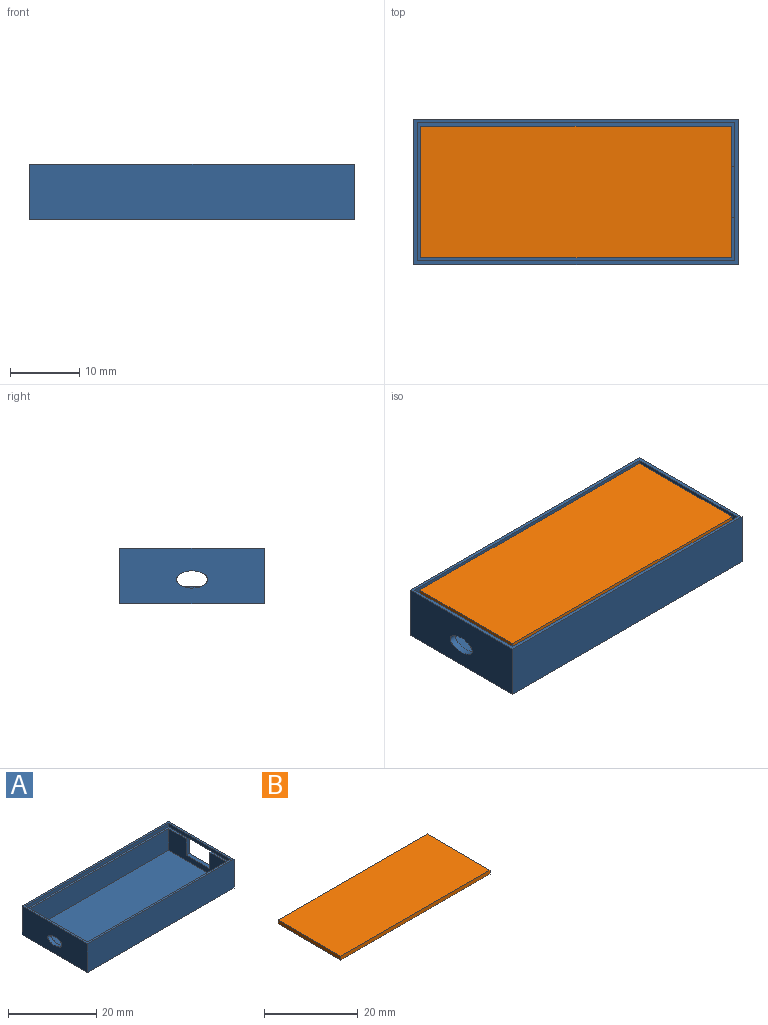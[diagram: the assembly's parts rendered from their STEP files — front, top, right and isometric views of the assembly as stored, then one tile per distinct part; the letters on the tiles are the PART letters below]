
ASSEMBLY  parts=2 mates=1
PART A: 21 faces, bbox 47x21x8 mm
  f0: plane 46x20mm, normal (0,0,1), area 61.3mm2, adj f2,f3,f4,f5,f7,f8,f9,f10
  f1: plane 21x8mm, normal (1,0,0), area 134.2mm2, adj f11,f13,f14,f15,f17,f18,f19,f20
  f2: plane 45x6mm, normal (0,-1,0), area 270mm2, adj f0,f3,f5,f6
  f3: plane 19x6mm, normal (1,0,0), area 105.2mm2, adj f0,f2,f4,f6,f16
  f4: plane 45x6mm, normal (0,1,0), area 270mm2, adj f0,f3,f5,f6
  f5: plane 19x6mm, normal (-1,0,0), area 80.3mm2, adj f0,f2,f4,f6,f17,f18,f19
  f6: plane 45x19mm, normal (0,0,1), area 855mm2, adj f2,f3,f4,f5
  f7: plane 46x1mm, normal (0,-1,0), area 46mm2, adj f0,f8,f10,f14
  f8: plane 20x1mm, normal (1,0,0), area 20mm2, adj f0,f7,f9,f14
  f9: plane 46x1mm, normal (0,1,0), area 46mm2, adj f0,f8,f10,f14
  f10: plane 20x1mm, normal (-1,0,0), area 20mm2, adj f0,f7,f9,f14,f20
  f11: plane 47x8mm, normal (0,1,0), area 376mm2, adj f1,f12,f14,f15
  f12: plane 21x8mm, normal (-1,0,0), area 159.2mm2, adj f11,f13,f14,f15,f16
  f13: plane 47x8mm, normal (0,-1,0), area 376mm2, adj f1,f12,f14,f15
  f14: plane 47x21mm, normal (0,0,1), area 67mm2, adj f1,f7,f8,f9,f10,f11,f12,f13
  f15: plane 47x21mm, normal (0,0,-1), area 987mm2, adj f1,f11,f12,f13
  f16: extruded ~4.5x2.5mm, area 11.2mm2, adj f3,f12
  f17: plane 4.5x1mm, normal (0,1,0), area 4.5mm2, adj f0,f1,f5,f18,f20
  f18: plane 7.5x1mm, normal (0,0,1), area 7.5mm2, adj f1,f5,f17,f19
  f19: plane 4.5x1mm, normal (0,-1,0), area 4.5mm2, adj f0,f1,f5,f18,f20
  f20: plane 7.5x0.5mm, normal (0,0,-1), area 3.8mm2, adj f1,f10,f17,f19
PART B: 6 faces, bbox 45x19x1 mm
  f0: plane 45x1mm, normal (0,1,0), area 45mm2, adj f1,f3,f4,f5
  f1: plane 19x1mm, normal (-1,0,0), area 19mm2, adj f0,f2,f4,f5
  f2: plane 45x1mm, normal (0,-1,0), area 45mm2, adj f1,f3,f4,f5
  f3: plane 19x1mm, normal (1,0,0), area 19mm2, adj f0,f2,f4,f5
  f4: plane 45x19mm, normal (0,0,1), area 855mm2, adj f0,f1,f2,f3
  f5: plane 45x19mm, normal (0,0,-1), area 855mm2, adj f0,f1,f2,f3
PLACE A t=(-0.25,32.6,0)mm
PLACE B t=(-0.25,32.6,7)mm
MATE fastened B.f1 <-> A.f3  axis (-1,0,0) through (-22.75,32.6,7.5)mm
